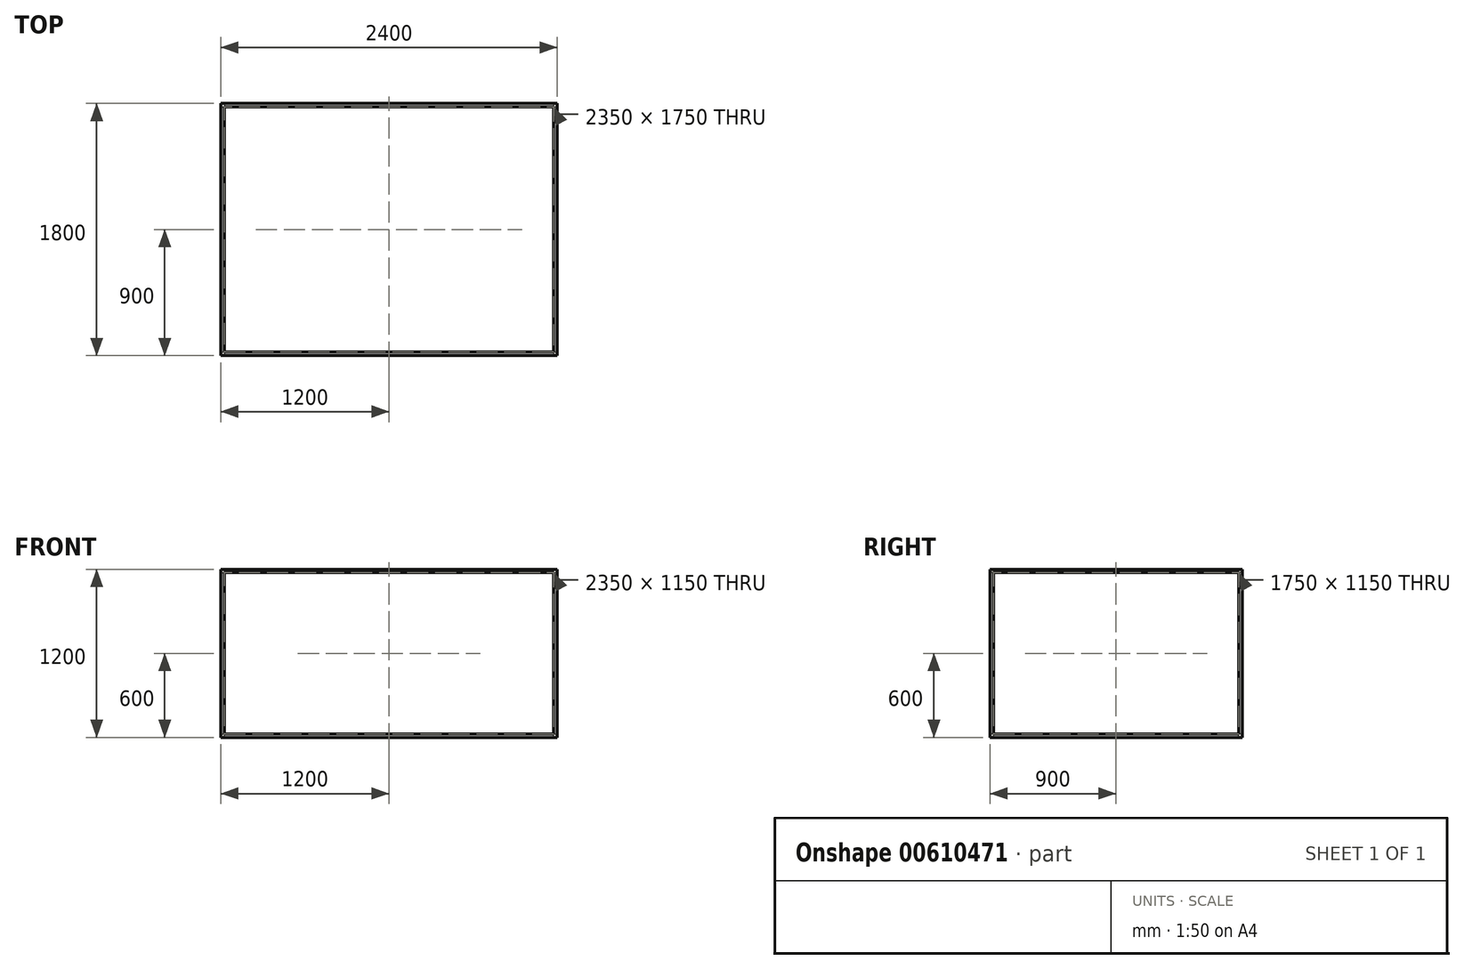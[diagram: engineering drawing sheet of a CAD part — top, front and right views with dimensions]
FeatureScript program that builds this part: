
annotation { "Feature Type Name" : "Feature", "Feature Type Description" : "" }
export const myFeature = defineFeature(function(context is Context, id is Id, definition is map)
    precondition{}
    {
        {
            var Q0;
            Q0=qCreatedBy(makeId("Front.planeOp"),FACE);
            var sketch = newSketch(context, id + "F0", { "sketchPlane" : qUnion([Q0])});
            skLineSegment(sketch, "E0.bottom", {"start": v(0, 0) * mm, "end": v(2400, 0) * mm});
            skLineSegment(sketch, "E0.top", {"start": v(0, 1200) * mm, "end": v(2400, 1200) * mm});
            skLineSegment(sketch, "E0.left", {"start": v(0, 0) * mm, "end": v(0, 1200) * mm});
            skLineSegment(sketch, "E0.right", {"start": v(2400, 0) * mm, "end": v(2400, 1200) * mm});
            skSolve(sketch);
        }
        {
            var Q0;
            Q0=makeQuery(id+"F0.imprint","IMPRINT",FACE,{"disambiguationData":[TD([[makeQuery(id+"F0.imprint","IMPRINT",EDGE,{"derivedFrom":sQuery(id+"F0.wireOp",EDGE,"E0.bottom")}),1.0]])]});
            extrude(context, id + "F1", {"entities" : qUnion([Q0]), "depth" : 1800 * mm, "offsetDistance" : 25 * mm});
        }
        {
            var Q0;
            Q0=makeQuery(id+"F1.opExtrude","CAP_FACE",FACE,{"disambiguationData":[OSD([sQuery(id+"F0.wireOp",EDGE,"E0.bottom"),sQuery(id+"F0.wireOp",EDGE,"E0.top"),sQuery(id+"F0.wireOp",EDGE,"E0.left"),sQuery(id+"F0.wireOp",EDGE,"E0.right")])],"isStart":false});
            var sketch = newSketch(context, id + "F2", { "sketchPlane" : qUnion([Q0])});
            skLineSegment(sketch, "E1.bottom", {"start": v(25, 1175) * mm, "end": v(2375, 1175) * mm});
            skLineSegment(sketch, "E1.top", {"start": v(25, 25) * mm, "end": v(2375, 25) * mm});
            skLineSegment(sketch, "E1.left", {"start": v(25, 1175) * mm, "end": v(25, 25) * mm});
            skLineSegment(sketch, "E1.right", {"start": v(2375, 1175) * mm, "end": v(2375, 25) * mm});
            skSolve(sketch);
        }
        {
            var Q0;
            Q0 = qSketchRegion(id + "F2", true);
            extrude(context, id + "F3", {"entities" : qUnion([Q0]), "operationType" : NewBodyOperationType.REMOVE, "endBound" : BoundingType.THROUGH_ALL, "oppositeDirection" : true, "depth" : 25 * mm, "offsetDistance" : 25 * mm});
        }
        {
            var Q0;
            Q0=makeQuery(id+"F1.opExtrude","SWEPT_FACE",FACE,{"disambiguationData":[OSD([sQuery(id+"F0.wireOp",EDGE,"E0.right")])]});
            var sketch = newSketch(context, id + "F4", { "sketchPlane" : qUnion([Q0])});
            skLineSegment(sketch, "E2.bottom", {"start": v(-1775, 25) * mm, "end": v(-25, 25) * mm});
            skLineSegment(sketch, "E2.top", {"start": v(-1775, 1175) * mm, "end": v(-25, 1175) * mm});
            skLineSegment(sketch, "E2.left", {"start": v(-1775, 25) * mm, "end": v(-1775, 1175) * mm});
            skLineSegment(sketch, "E2.right", {"start": v(-25, 25) * mm, "end": v(-25, 1175) * mm});
            skSolve(sketch);
        }
        {
            var Q0;
            Q0 = qSketchRegion(id + "F4", true);
            extrude(context, id + "F5", {"entities" : qUnion([Q0]), "operationType" : NewBodyOperationType.REMOVE, "endBound" : BoundingType.THROUGH_ALL, "oppositeDirection" : true, "depth" : 25 * mm, "offsetDistance" : 25 * mm});
        }
        {
            var Q0;
            Q0=makeQuery(id+"F1.opExtrude","SWEPT_FACE",FACE,{"disambiguationData":[OSD([sQuery(id+"F0.wireOp",EDGE,"E0.top")])]});
            var sketch = newSketch(context, id + "F6", { "sketchPlane" : qUnion([Q0])});
            skLineSegment(sketch, "E3.bottom", {"start": v(25, -25) * mm, "end": v(2375, -25) * mm});
            skLineSegment(sketch, "E3.top", {"start": v(25, -1775) * mm, "end": v(2375, -1775) * mm});
            skLineSegment(sketch, "E3.left", {"start": v(25, -25) * mm, "end": v(25, -1775) * mm});
            skLineSegment(sketch, "E3.right", {"start": v(2375, -25) * mm, "end": v(2375, -1775) * mm});
            skSolve(sketch);
        }
        {
            var Q0;
            Q0 = qSketchRegion(id + "F6", true);
            extrude(context, id + "F7", {"entities" : qUnion([Q0]), "operationType" : NewBodyOperationType.REMOVE, "endBound" : BoundingType.THROUGH_ALL, "oppositeDirection" : true, "depth" : 25 * mm, "offsetDistance" : 25 * mm});
        }
    });
